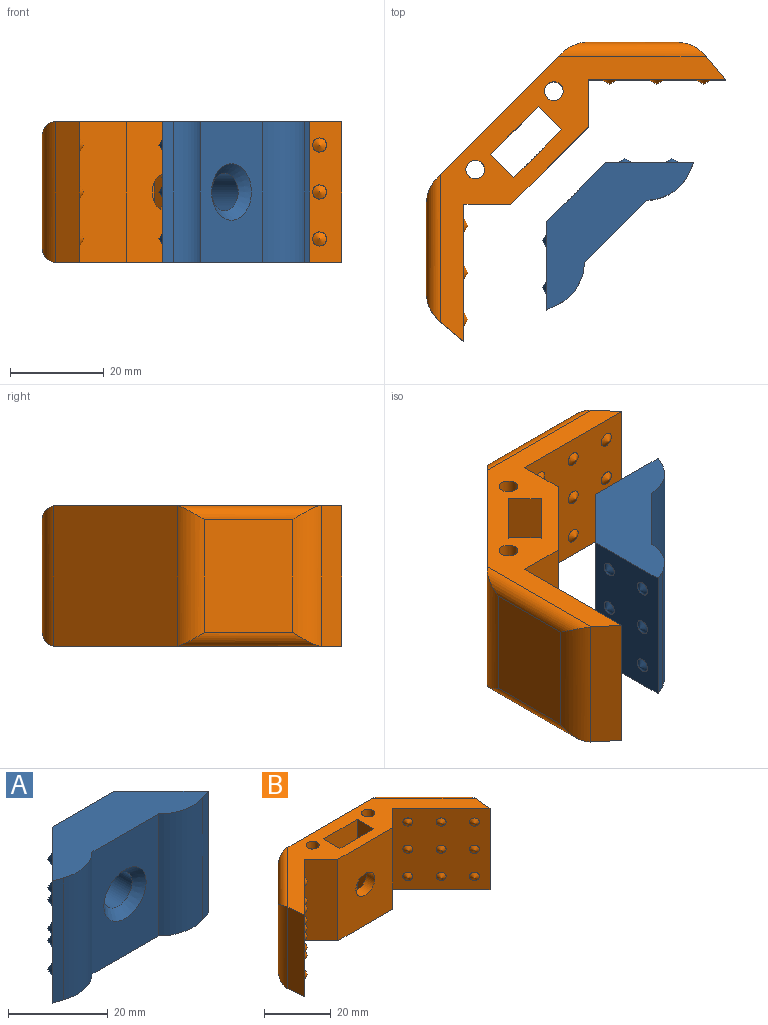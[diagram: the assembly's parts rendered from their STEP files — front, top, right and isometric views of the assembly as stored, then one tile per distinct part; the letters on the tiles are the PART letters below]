
ASSEMBLY  parts=2 mates=1
PART A: 24 faces, bbox 44.3x14.7x30 mm
  f0: plane 30x18.77mm, normal (0,-1,0), area 450mm2, adj f6,f7,f9,f10,f11
  f1: plane 30x2.37mm, normal (0.34,-0.94,0), area 75.6mm2, adj f2,f6,f7,f11
  f2: plane 30x13.29mm, normal (0.71,0.71,0), area 521.2mm2, adj f1,f3,f6,f7,f18,f19,f20,f21
  f3: plane 30x17.74mm, normal (0,1,0), area 481.8mm2, adj f2,f4,f6,f7,f8
  f4: plane 30x13.29mm, normal (-0.71,0.71,0), area 521.2mm2, adj f3,f5,f6,f7,f12,f13,f14,f15
  f5: plane 30x2.37mm, normal (-0.34,-0.94,0), area 75.6mm2, adj f4,f6,f7,f10
  f6: plane 44.31x14.72mm, normal (0,0,1), area 402.7mm2, adj f0,f1,f2,f3,f4,f5,f10,f11
  f7: plane 44.31x14.72mm, normal (0,0,-1), area 402.7mm2, adj f0,f1,f2,f3,f4,f5,f10,f11
  f8: cylinder r=4mm len=9.83mm, axis (0,-1,0), area 247.1mm2, adj f3,f9
  f9: cone r=4mm half-angle=45deg, axis (0,-1,0), area 88.9mm2, adj f0,f8
  f10: cylinder r=10mm len=30mm, axis (0,0,1), area 336.9mm2, adj f0,f5,f6,f7
  f11: cylinder r=10mm len=30mm, axis (0,0,1), area 336.9mm2, adj f0,f1,f6,f7
  f12: cone r=1.5mm half-angle=60deg, axis (0.71,-0.71,0), area 8.2mm2, adj f4
  f13: cone r=1.5mm half-angle=60deg, axis (0.71,-0.71,0), area 8.2mm2, adj f4
  f14: cone r=1.5mm half-angle=60deg, axis (0.71,-0.71,0), area 8.2mm2, adj f4
  f15: cone r=1.5mm half-angle=60deg, axis (0.71,-0.71,0), area 8.2mm2, adj f4
  f16: cone r=1.5mm half-angle=60deg, axis (0.71,-0.71,0), area 8.2mm2, adj f4
  f17: cone r=1.5mm half-angle=60deg, axis (0.71,-0.71,0), area 8.2mm2, adj f4
  f18: cone r=1.5mm half-angle=60deg, axis (-0.71,-0.71,0), area 8.2mm2, adj f2
  f19: cone r=1.5mm half-angle=60deg, axis (-0.71,-0.71,0), area 8.2mm2, adj f2
  f20: cone r=1.5mm half-angle=60deg, axis (-0.71,-0.71,0), area 8.2mm2, adj f2
  f21: cone r=1.5mm half-angle=60deg, axis (-0.71,-0.71,0), area 8.2mm2, adj f2
  f22: cone r=1.5mm half-angle=60deg, axis (-0.71,-0.71,0), area 8.2mm2, adj f2
  f23: cone r=1.5mm half-angle=60deg, axis (-0.71,-0.71,0), area 8.2mm2, adj f2
PART B: 47 faces, bbox 84.2x30.8x30 mm
  f0: plane 30x6.64mm, normal (1,-0.09,0), area 200.1mm2, adj f13,f16,f17,f21,f27,f28
  f1: plane 24x13.31mm, normal (0.71,0.71,0), area 451.6mm2, adj f21,f22,f27,f28
  f2: plane 37.46x30mm, normal (0,1,0), area 1123.6mm2, adj f16,f17,f22,f23,f25,f26,f27,f28
  f3: plane 24x13.31mm, normal (-0.71,0.71,0), area 451.6mm2, adj f23,f24,f25,f26
  f4: plane 30x6.64mm, normal (-1,-0.09,0), area 200.1mm2, adj f5,f16,f17,f24,f25,f26
  f5: plane 30x20.67mm, normal (0.71,-0.71,0), area 813.4mm2, adj f4,f6,f16,f17,f29,f30,f31,f32
  f6: plane 30x7.07mm, normal (-0.71,-0.71,0), area 300mm2, adj f5,f7,f16,f17
  f7: plane 30x23.31mm, normal (0,-1,0), area 649.1mm2, adj f6,f8,f16,f17,f20
  f8: plane 30x7.07mm, normal (0.71,-0.71,0), area 300mm2, adj f7,f13,f16,f17
  f9: plane 30x7mm, normal (-1,0,0), area 210mm2, adj f10,f14,f16,f17
  f10: plane 30x14.4mm, normal (0,1,0), area 381.7mm2, adj f9,f11,f16,f17,f20
  f11: plane 30x7mm, normal (1,0,0), area 210mm2, adj f10,f14,f16,f17
  f12: cylinder r=2mm len=30mm, axis (0,0,-1), area 377mm2, adj f16,f17
  f13: plane 30x20.67mm, normal (-0.71,-0.71,0), area 813.4mm2, adj f0,f8,f16,f17,f38,f39,f40,f41
  f14: plane 30x14.4mm, normal (0,-1,0), area 381.7mm2, adj f9,f11,f16,f17,f19
  f15: cylinder r=2mm len=30mm, axis (0,0,-1), area 377mm2, adj f16,f17
  f16: plane 79.97x28.67mm, normal (0,0,1), area 684.2mm2, adj f0,f2,f4,f5,f6,f7,f8,f9
  f17: plane 79.97x28.67mm, normal (0,0,-1), area 684.2mm2, adj f0,f2,f4,f5,f6,f7,f8,f9
  f18: cone r=0mm half-angle=59deg, axis (0,-1,0), area 58.6mm2, adj f19
  f19: cylinder r=4mm len=8mm, axis (0,-1,0), area 27mm2, adj f14,f18
  f20: cylinder r=4mm len=8mm, axis (0,-1,0), area 89.8mm2, adj f7,f10
  f21: cylinder r=8mm len=30mm, axis (0,0,-1), area 193.8mm2, adj f0,f1,f27,f28
  f22: cylinder r=8mm len=29.85mm, axis (0,0,-1), area 172.1mm2, adj f1,f2,f27,f28
  f23: cylinder r=8mm len=29.85mm, axis (0,0,1), area 172.1mm2, adj f2,f3,f25,f26
  f24: cylinder r=8mm len=30mm, axis (0,0,-1), area 193.8mm2, adj f3,f4,f25,f26
  f25: cylinder r=3mm len=24.31mm, axis (0.71,0.71,0), area 121.4mm2, adj f2,f3,f4,f16,f23,f24
  f26: cylinder r=3mm len=24.31mm, axis (-0.71,-0.71,0), area 121.4mm2, adj f2,f3,f4,f17,f23,f24
  f27: cylinder r=3mm len=24.31mm, axis (0.71,-0.71,0), area 121.4mm2, adj f0,f1,f2,f16,f21,f22
  f28: cylinder r=3mm len=24.31mm, axis (-0.71,0.71,0), area 121.4mm2, adj f0,f1,f2,f17,f21,f22
  f29: cone r=1.5mm half-angle=60deg, axis (-0.71,0.71,0), area 8.2mm2, adj f5
  f30: cone r=1.5mm half-angle=60deg, axis (-0.71,0.71,0), area 8.2mm2, adj f5
  f31: cone r=1.5mm half-angle=60deg, axis (-0.71,0.71,0), area 8.2mm2, adj f5
  f32: cone r=1.5mm half-angle=60deg, axis (-0.71,0.71,0), area 8.2mm2, adj f5
  f33: cone r=1.5mm half-angle=60deg, axis (-0.71,0.71,0), area 8.2mm2, adj f5
  f34: cone r=1.5mm half-angle=60deg, axis (-0.71,0.71,0), area 8.2mm2, adj f5
  f35: cone r=1.5mm half-angle=60deg, axis (-0.71,0.71,0), area 8.2mm2, adj f5
  f36: cone r=1.5mm half-angle=60deg, axis (-0.71,0.71,0), area 8.2mm2, adj f5
  f37: cone r=1.5mm half-angle=60deg, axis (-0.71,0.71,0), area 8.2mm2, adj f5
  f38: cone r=1.5mm half-angle=60deg, axis (0.71,0.71,0), area 8.2mm2, adj f13
  f39: cone r=1.5mm half-angle=60deg, axis (0.71,0.71,0), area 8.2mm2, adj f13
  f40: cone r=1.5mm half-angle=60deg, axis (0.71,0.71,0), area 8.2mm2, adj f13
  f41: cone r=1.5mm half-angle=60deg, axis (0.71,0.71,0), area 8.2mm2, adj f13
  f42: cone r=1.5mm half-angle=60deg, axis (0.71,0.71,0), area 8.2mm2, adj f13
  f43: cone r=1.5mm half-angle=60deg, axis (0.71,0.71,0), area 8.2mm2, adj f13
  f44: cone r=1.5mm half-angle=60deg, axis (0.71,0.71,0), area 8.2mm2, adj f13
  f45: cone r=1.5mm half-angle=60deg, axis (0.71,0.71,0), area 8.2mm2, adj f13
  f46: cone r=1.5mm half-angle=60deg, axis (0.71,0.71,0), area 8.2mm2, adj f13
PLACE A rot(axis=(0,0,1),45deg) t=(-233.5,-208.7,187.91)mm
PLACE B rot(axis=(0.38,-0.92,0),180deg) t=(-237.72,-204.48,217.91)mm
MATE fastened A.f8 <-> B.f18  axis (-0.71,0.71,0) through (-236.06,-206.13,202.91)mm
